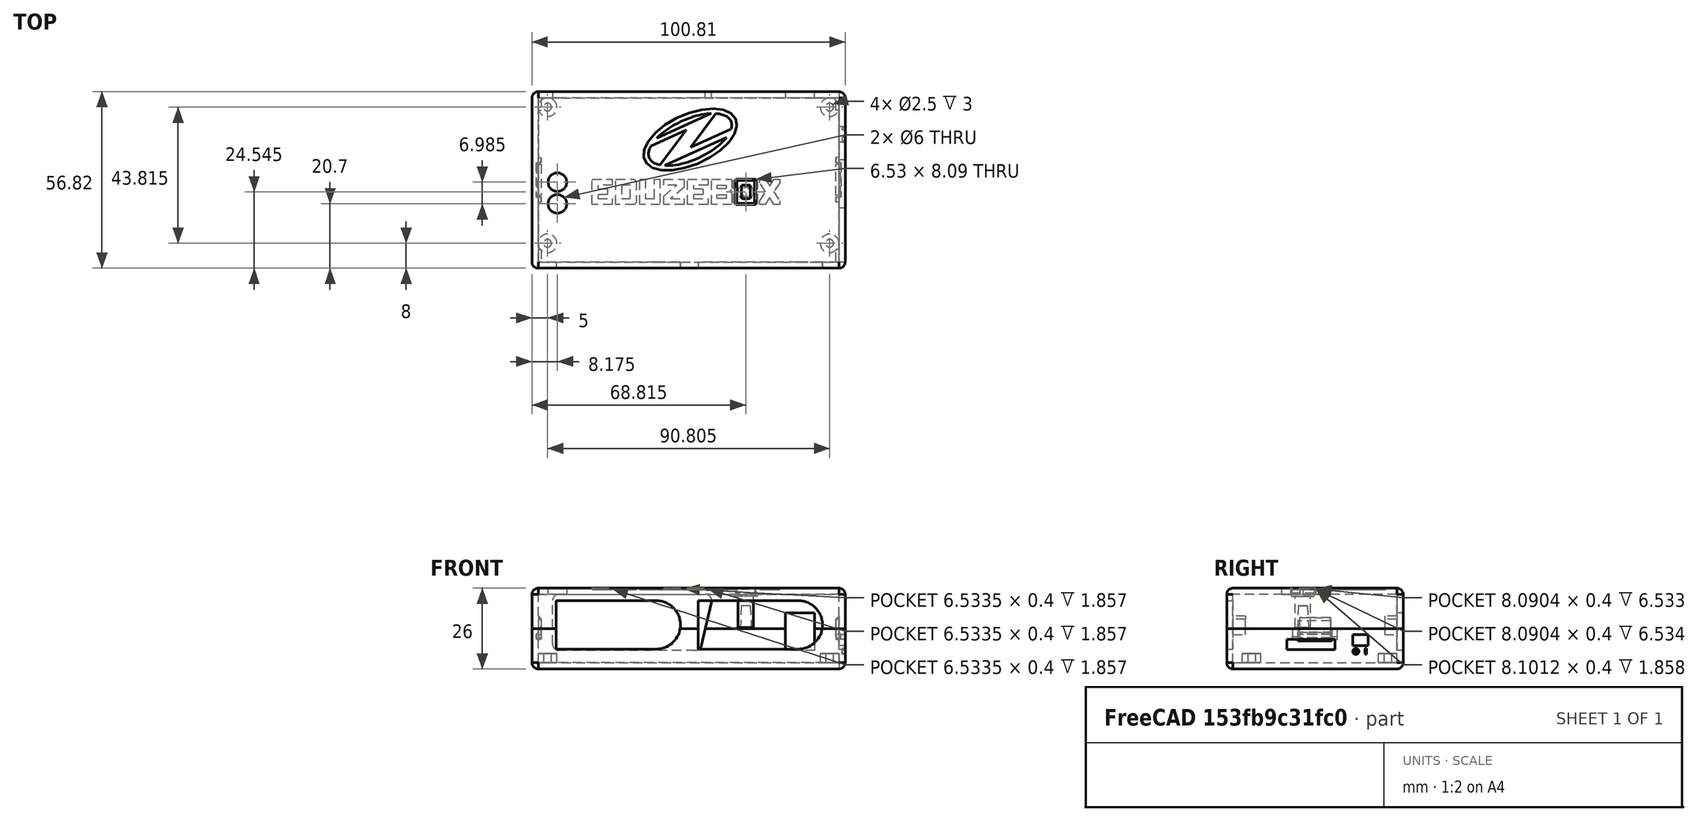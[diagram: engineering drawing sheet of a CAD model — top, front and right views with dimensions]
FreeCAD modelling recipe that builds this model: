
FCSTD DOCUMENT  (FreeCAD 0.18.4R)
Label: case
License: CreativeCommons Attribution-ShareAlike
LicenseURL: http://creativecommons.org/licenses/by-sa/4.0/
objects: Part::Extrusion×41, Part::Cut×38, Part::Part2DObjectPython×31, Part::FeaturePython×17, Part::Feature×11, Part::Fuse×10, Part::MultiFuse×6, Part::Thickness×2, Part::Chamfer×2, Part::Cone×1, Part::Cylinder×1
note: 160 computed .brp shape members not serialized (recipe doc carries the construction recipe); baked Part::Feature solids carry a one-line shape summary decoded from their .brp

FEATURE [Part::Part2DObjectPython] Block  label="PCB"  # Draft 2D object (typed FeaturePython)
  Placement = pos=(-88.9,107.95,0) rot=(0,0,1;0rad)
FEATURE [Part::Part2DObjectPython] Circle  # Draft 2D object (typed FeaturePython)
  FirstAngle = 0
  LastAngle = 0
  MakeFace = true
  Placement = pos=(2.54,2.54,-1.6) rot=(1,0,0;3.14159rad)
  Radius = 3
  Support = -> [Block]
FEATURE [Part::Extrusion] Extrude
  Base = -> Circle
  Dir = (0,0,-1)
  DirMode = 2
  FaceMakerClass = Part::FaceMakerBullseye
  LengthFwd = 3
  LengthRev = 0
  Solid = false
  Symmetric = false
FEATURE [Part::Part2DObjectPython] Circle001  # Draft 2D object (typed FeaturePython)
  FirstAngle = 0
  LastAngle = 0
  MakeFace = true
  Placement = pos=(2.54,2.54,-4.6) rot=(1,0,0;3.14159rad)
  Radius = 1.25
  Support = -> [Extrude]
FEATURE [Part::Extrusion] Extrude001  label="agujero"
  Base = -> Circle001
  Dir = (0,0,-1)
  DirMode = 2
  FaceMakerClass = Part::FaceMakerBullseye
  LengthFwd = -3
  LengthRev = 0
  Solid = false
  Symmetric = false
FEATURE [Part::Cut] Cut  label="Apoyo1"
  Base = -> Extrude
  Refine = true
  Tool = -> Extrude001
FEATURE [Part::FeaturePython] Clone  label="Apoyo2"  # Draft clone (typed FeaturePython)
  AttacherType = Attacher::AttachEngine3D
  Fuse = false
  Objects = -> [Cut]
  Placement = pos=(0,43.815,0) rot=(0,0,1;0rad)
  Scale = (1,1,1)
FEATURE [Part::FeaturePython] Clone001  label="Apoyo3"  # Draft clone (typed FeaturePython)
  AttacherType = Attacher::AttachEngine3D
  Fuse = false
  Objects = -> [Clone]
  Placement = pos=(90.805,43.815,0) rot=(0,0,1;0rad)
  Scale = (1,1,1)
FEATURE [Part::FeaturePython] Clone002  label="Apoyo4"  # Draft clone (typed FeaturePython)
  AttacherType = Attacher::AttachEngine3D
  Fuse = false
  Objects = -> [Clone001]
  Placement = pos=(90.805,0,0) rot=(0,0,1;0rad)
  Scale = (1,1,1)
FEATURE [Part::Part2DObjectPython] Rectangle  # Draft 2D object (typed FeaturePython)
  ChamferSize = 0
  Columns = 1
  FilletRadius = 0
  Height = 52.81
  Length = 96.805
  MakeFace = true
  Placement = pos=(-0.46,49.355,-4.6) rot=(1,0,0;3.14159rad)
  Rows = 1
FEATURE [Part::Extrusion] Extrude002
  Base = -> Rectangle
  Dir = (0,0,-1)
  DirMode = 2
  FaceMakerClass = Part::FaceMakerBullseye
  LengthFwd = -11
  LengthRev = 0
  Solid = false
  Symmetric = false
FEATURE [Part::Part2DObjectPython] Rectangle001  # Draft 2D object (typed FeaturePython)
  ChamferSize = 0
  Columns = 1
  FilletRadius = 0
  Height = 3.3
  Length = 15.5
  MakeFace = true
  Placement = pos=(98.345,13.93,-0.4) rot=(0.57735,0.57735,0.57735;2.0944rad)
  Rows = 1
FEATURE [Part::Extrusion] Extrude005  label="HuecoSD"
  Base = -> Rectangle001
  Dir = (1,0,0)
  DirMode = 2
  FaceMakerClass = Part::FaceMakerBullseye
  LengthFwd = -3
  LengthRev = 0
  Solid = false
  Symmetric = false
FEATURE [Part::Part2DObjectPython] Rectangle002  # Draft 2D object (typed FeaturePython)
  ChamferSize = 0
  Columns = 1
  FilletRadius = 0
  Height = 3.5
  Length = 5
  MakeFace = true
  Placement = pos=(98.345,35.06,0.9) rot=(0.57735,0.57735,0.57735;2.0944rad)
  Rows = 1
FEATURE [Part::Extrusion] Extrude006  label="HuecoOnOff"
  Base = -> Rectangle002
  Dir = (1,0,0)
  DirMode = 2
  FaceMakerClass = Part::FaceMakerBullseye
  LengthFwd = -3
  LengthRev = 0
  Solid = false
  Symmetric = false
FEATURE [Part::Part2DObjectPython] Rectangle003  # Draft 2D object (typed FeaturePython)
  ChamferSize = 0
  Columns = 1
  FilletRadius = 0
  Height = 12
  Length = 9.4
  MakeFace = true
  Placement = pos=(88.52,51.355,-0.6) rot=(0,0.707107,0.707107;3.14159rad)
  Rows = 1
FEATURE [Part::Extrusion] Extrude007  label="HuecoPower"
  Base = -> Rectangle003
  Dir = (0,1,-2e-16)
  DirMode = 2
  FaceMakerClass = Part::FaceMakerBullseye
  LengthFwd = -3
  LengthRev = 0
  Solid = false
  Symmetric = false
FEATURE [Part::Part2DObjectPython] Rectangle004  # Draft 2D object (typed FeaturePython)
  ChamferSize = 0
  Columns = 1
  FilletRadius = 0
  Height = 1.98134
  Length = 0.517414
  MakeFace = true
  Placement = pos=(98.345,39.0982,-1.9384) rot=(0.57735,0.57735,0.57735;2.0944rad)
  Rows = 1
FEATURE [Part::Extrusion] Extrude009  label="On"
  Base = -> Rectangle004
  Dir = (1,0,0)
  DirMode = 2
  FaceMakerClass = Part::FaceMakerBullseye
  LengthFwd = -1
  LengthRev = 0
  Solid = false
  Symmetric = false
FEATURE [Part::Part2DObjectPython] Circle002  # Draft 2D object (typed FeaturePython)
  FirstAngle = 0
  LastAngle = 0
  MakeFace = true
  Placement = pos=(98.345,36.126,-0.947734) rot=(0.57735,0.57735,0.57735;2.0944rad)
  Radius = 0.990671
FEATURE [Part::Extrusion] Extrude010  label="ExteriorOff"
  Base = -> Circle002
  Dir = (1,0,0)
  DirMode = 2
  FaceMakerClass = Part::FaceMakerBullseye
  LengthFwd = -1
  LengthRev = 0
  Solid = false
  Symmetric = false
FEATURE [Part::Part2DObjectPython] Circle003  # Draft 2D object (typed FeaturePython)
  FirstAngle = 0
  LastAngle = 0
  MakeFace = true
  Placement = pos=(98.345,36.126,-0.947734) rot=(0.57735,0.57735,0.57735;2.0944rad)
  Radius = 0.5
FEATURE [Part::Extrusion] Extrude011  label="InteriorOff"
  Base = -> Circle003
  Dir = (1,0,0)
  DirMode = 2
  FaceMakerClass = Part::FaceMakerBullseye
  LengthFwd = -1
  LengthRev = 0
  Solid = false
  Symmetric = false
FEATURE [Part::Part2DObjectPython] Rectangle005  # Draft 2D object (typed FeaturePython)
  ChamferSize = 0
  Columns = 1
  FilletRadius = 0
  Height = 52.81
  Length = 96.805
  MakeFace = true
  Placement = pos=(-0.46,-3.455,6.4) rot=(0,0,1;0rad)
  Rows = 1
FEATURE [Part::Extrusion] Extrude012
  Base = -> Rectangle005
  Dir = (0,0,1)
  DirMode = 2
  FaceMakerClass = Part::FaceMakerBullseye
  LengthFwd = 11
  LengthRev = 0
  Solid = false
  Symmetric = false
FEATURE [Part::Thickness] Thickness001
  Faces = -> Extrude012 [Face5]
  Intersection = false
  Join = 0
  Mode = 0
  SelfIntersection = false
  Value = 2
FEATURE [Part::Feature] Face003
  shape: bbox 55.45 x 2.007e-07 x 20.64 mm, 1 faces, 0 solids (baked)
FEATURE [Part::Extrusion] Extrude013  label="HuecoSCART2"
  Base = -> Face003
  Dir = (0,1,0)
  DirMode = 0
  FaceMakerClass = Part::FaceMakerBullseye
  LengthFwd = -2
  LengthRev = 0
  Solid = false
  Symmetric = false
FEATURE [Part::Feature] Face004
  shape: bbox 43.88 x 1.599e-05 x 17.16 mm, 1 faces, 0 solids (baked)
FEATURE [Part::Extrusion] Extrude014  label="HuecoPortA"
  Base = -> Face004
  Dir = (0,1,0)
  DirMode = 0
  FaceMakerClass = Part::FaceMakerBullseye
  LengthFwd = 2
  LengthRev = 0
  Solid = false
  Symmetric = false
FEATURE [Part::Thickness] Thickness
  Faces = -> Extrude002 [Face6]
  Intersection = false
  Join = 0
  Mode = 0
  SelfIntersection = false
  Value = 2
FEATURE [Part::FeaturePython] Clone003  label="HuecoPortB"  # Draft clone (typed FeaturePython)
  AttacherType = Attacher::AttachEngine3D
  Fuse = false
  Objects = -> [Extrude014]
  Placement = pos=(45.72,-7.62939e-08,2.98023e-09) rot=(0,0,1;0rad)
  Scale = (1,1,1)
FEATURE [Part::Cut] Cut001
  Base = -> Thickness
  Refine = true
  Tool = -> Extrude014
FEATURE [Part::Cut] Cut002
  Base = -> Cut001
  Refine = true
  Tool = -> Clone003
FEATURE [Part::Cut] Cut003
  Base = -> Cut002
  Refine = true
  Tool = -> Extrude005
FEATURE [Part::Cut] Cut004
  Base = -> Cut003
  Refine = true
  Tool = -> Extrude006
FEATURE [Part::Cut] Cut005
  Base = -> Cut004
  Refine = true
  Tool = -> Extrude010
FEATURE [Part::Cut] Cut006
  Base = -> Cut005
  Refine = true
  Tool = -> Extrude009
FEATURE [Part::Cut] Cut007
  Base = -> Cut006
  Refine = true
  Tool = -> Extrude007
FEATURE [Part::Cut] Cut008
  Base = -> Cut007
  Refine = true
  Tool = -> Extrude013
FEATURE [Part::Cut] Cut009
  Base = -> Thickness001
  Refine = true
  Tool = -> Extrude014
FEATURE [Part::Cut] Cut010
  Base = -> Cut009
  Refine = true
  Tool = -> Clone003
FEATURE [Part::Cut] Cut011
  Base = -> Cut010
  Refine = true
  Tool = -> Extrude007
FEATURE [Part::Cut] Cut012
  Base = -> Cut011
  Refine = true
  Tool = -> Extrude013
FEATURE [Part::Part2DObjectPython] Circle004  # Draft 2D object (typed FeaturePython)
  FirstAngle = 0
  LastAngle = 0
  MakeFace = true
  Placement = pos=(5.715,22.225,19.4) rot=(0,0,1;0rad)
  Radius = 2.5
  Support = -> [Cut012]
FEATURE [Part::Part2DObjectPython] Circle005  # Draft 2D object (typed FeaturePython)
  FirstAngle = 0
  LastAngle = 0
  MakeFace = true
  Placement = pos=(5.715,15.24,19.4) rot=(0,0,1;0rad)
  Radius = 2.5
FEATURE [Part::Extrusion] Extrude015  label="HuecoLEDRojo"
  Base = -> Circle004
  Dir = (0,0,1)
  DirMode = 2
  FaceMakerClass = Part::FaceMakerBullseye
  LengthFwd = -2
  LengthRev = 0
  Solid = false
  Symmetric = false
FEATURE [Part::Extrusion] Extrude016  label="HuecoLEDAzul"
  Base = -> Circle005
  Dir = (0,0,1)
  DirMode = 2
  FaceMakerClass = Part::FaceMakerBullseye
  LengthFwd = -2
  LengthRev = 0
  Solid = false
  Symmetric = false
FEATURE [Part::Cut] Cut013
  Base = -> Cut012
  Refine = true
  Tool = -> Extrude015
FEATURE [Part::Cut] Cut014
  Base = -> Cut013
  Refine = true
  Tool = -> Extrude016
FEATURE [Part::Part2DObjectPython] Wire  label="LogoU"  # Draft 2D object (typed FeaturePython)
  ChamferSize = 0
  Closed = true
  End = (31.5108,15.0742,19.4)
  FilletRadius = 0
  Length = 41.7617
  MakeFace = true
  Placement = pos=(31.5108,23.1754,19.4) rot=(0,0,1;0rad)
  Points = (8) [(0,0,0),(1.85748,0,0),(1.86285,-6.24368,0),(4.68122,-6.24368,0),(4.68122,0,0),(6.5387,0,0),(6.5387,-8.10116,0),(0,-8.10116,0)]
  Start = (31.5108,23.1754,19.4)
  Subdivisions = 0
FEATURE [Part::Part2DObjectPython] Wire001  label="LogoZ"  # Draft 2D object (typed FeaturePython)
  ChamferSize = 0
  Closed = true
  End = (39.2449,21.3179,19.4)
  FilletRadius = 0
  Length = 41.9129
  MakeFace = true
  Placement = pos=(39.2449,23.1754,19.4) rot=(0,0,1;0rad)
  Points = (10) [(0,0,0),(6.53352,0,0),(6.53352,-2.67345,0),(2.22794,-6.23293,0),(6.53352,-6.23293,0),(6.53352,-8.09041,0),(0,-8.09041,0),(0,-5.41676,0),+2 more]
  Start = (39.2449,23.1754,19.4)
  Subdivisions = 0
FEATURE [Part::Part2DObjectPython] Wire002  label="LogoE2"  # Draft 2D object (typed FeaturePython)
  ChamferSize = 0
  Closed = true
  End = (46.9353,15.085,19.4)
  FilletRadius = 0
  Length = 44.6982
  MakeFace = true
  Placement = pos=(46.9353,23.1754,19.4) rot=(0,0,1;0rad)
  Points = (12) [(0,0,0),(6.53352,0,0),(6.53352,-1.85748,0),(1.85767,-1.85748,0),(1.85767,-3.11915,0),(4.97663,-3.11915,0),(4.97663,-4.97125,0),(1.93272,-4.97125,0),+4 more]
  Start = (46.9353,23.1754,19.4)
  Subdivisions = 0
FEATURE [Part::Part2DObjectPython] Wire003  label="LogoB0"  # Draft 2D object (typed FeaturePython)
  ChamferSize = 0
  Closed = true
  End = (54.6335,15.085,19.4)
  FilletRadius = 0
  Length = 29.7435
  MakeFace = true
  Placement = pos=(54.6335,23.1754,19.4) rot=(0,0,1;0rad)
  Points = (7) [(0,0,0),(6.53352,0,0),(6.54964,-3.39824,0),(5.93771,-4.01036,0),(6.53352,-4.62229,0),(6.53352,-8.09041,0),(0,-8.09041,0)]
  Start = (54.6335,23.1754,19.4)
  Subdivisions = 0
FEATURE [Part::Part2DObjectPython] Wire004  label="LogoB1"  # Draft 2D object (typed FeaturePython)
  ChamferSize = 0
  Closed = true
  End = (56.4912,20.0563,19.4)
  FilletRadius = 0
  Length = 8.16008
  MakeFace = true
  Placement = pos=(56.4912,21.3179,19.4) rot=(0,0,1;0rad)
  Points = (4) [(0,0,0),(2.81837,0,0),(2.81837,-1.26167,0),(0,-1.26167,0)]
  Start = (56.4912,21.3179,19.4)
  Subdivisions = 0
FEATURE [Part::Part2DObjectPython] Wire005  label="LogoB2"  # Draft 2D object (typed FeaturePython)
  ChamferSize = 0
  Closed = true
  End = (56.4912,16.9425,19.4)
  FilletRadius = 0
  Length = 8.16008
  MakeFace = true
  Placement = pos=(56.4912,18.2042,19.4) rot=(0,0,1;0rad)
  Points = (4) [(0,0,0),(2.81837,0,0),(2.81837,-1.26167,0),(0,-1.26167,0)]
  Start = (56.4912,18.2042,19.4)
  Subdivisions = 0
FEATURE [Part::Part2DObjectPython] Wire006  label="LogoX"  # Draft 2D object (typed FeaturePython)
  ChamferSize = 0
  Closed = true
  End = (70.7859,22.0694,19.4)
  FilletRadius = 0
  Length = 36.5598
  MakeFace = true
  Placement = pos=(70.7859,23.1862,19.4) rot=(0,0,1;0rad)
  Points = (16) [(0,0,0),(1.85748,0,0),(3.3017,-2.21719,0),(4.68142,0,0),(6.5389,0,0),(6.5389,-1.11675,0),(4.53112,-4.01574,0),(6.5389,-6.98441,0),(6.5389,-8.10116,0),+7 more]
  Start = (70.7859,23.1862,19.4)
  Subdivisions = 0
FEATURE [Part::Part2DObjectPython] Rectangle006  label="LogoD1"  # Draft 2D object (typed FeaturePython)
  ChamferSize = 0
  Columns = 1
  FilletRadius = 0
  Height = 4.37545
  Length = 2.81837
  MakeFace = true
  Placement = pos=(25.727,16.9425,19.4) rot=(0,0,1;0rad)
  Rows = 1
FEATURE [Part::Feature] Face  label="LogoD0"
  Placement = pos=(12.3152,-43.294,-3.8147e-07) rot=(0,0,1;0rad)
  shape: bbox 7.217 x 8.924 x 2e-07 mm, 1 faces, 0 solids (baked)
FEATURE [Part::Part2DObjectPython] Clone2D  label="LogoE1"  # Draft 2D object (typed FeaturePython)
  Fuse = false
  Objects = -> [Wire002]
  Placement = pos=(16.1868,23.1754,19.4) rot=(0,0,1;0rad)
  Scale = (1,1,1)
FEATURE [Part::Extrusion] Extrude018  label="LogoE1_v"
  Base = -> Clone2D
  Dir = (0,0,1)
  DirMode = 2
  FaceMakerClass = Part::FaceMakerBullseye
  LengthFwd = -0.4
  LengthRev = 0
  Placement = pos=(0.680956,0,0) rot=(0,0,1;0rad)
  Solid = false
  Symmetric = false
FEATURE [Part::Extrusion] Extrude019  label="LogoD0_v"
  Base = -> Face
  Dir = (0,0,-1)
  DirMode = 0
  FaceMakerClass = Part::FaceMakerBullseye
  LengthFwd = 0.4
  LengthRev = 0
  Placement = pos=(0.680956,0,0) rot=(0,0,1;0rad)
  Solid = false
  Symmetric = false
FEATURE [Part::Extrusion] Extrude020  label="LogoD1_v"
  Base = -> Rectangle006
  Dir = (0,0,1)
  DirMode = 2
  FaceMakerClass = Part::FaceMakerBullseye
  LengthFwd = -0.4
  LengthRev = 0
  Placement = pos=(0.680956,0,0) rot=(0,0,1;0rad)
  Solid = false
  Symmetric = false
FEATURE [Part::Extrusion] Extrude021  label="LogoU_v"
  Base = -> Wire
  Dir = (0,0,1)
  DirMode = 2
  FaceMakerClass = Part::FaceMakerBullseye
  LengthFwd = -0.4
  LengthRev = 0
  Placement = pos=(0.680956,0,0) rot=(0,0,1;0rad)
  Solid = false
  Symmetric = false
FEATURE [Part::Extrusion] Extrude022  label="LogoZ_v"
  Base = -> Wire001
  Dir = (0,0,1)
  DirMode = 2
  FaceMakerClass = Part::FaceMakerBullseye
  LengthFwd = -0.4
  LengthRev = 0
  Placement = pos=(0.680956,0,0) rot=(0,0,1;0rad)
  Solid = false
  Symmetric = false
FEATURE [Part::Extrusion] Extrude023  label="LogoE2_v"
  Base = -> Wire002
  Dir = (0,0,1)
  DirMode = 2
  FaceMakerClass = Part::FaceMakerBullseye
  LengthFwd = -0.4
  LengthRev = 0
  Placement = pos=(0.680956,0,0) rot=(0,0,1;0rad)
  Solid = false
  Symmetric = false
FEATURE [Part::Extrusion] Extrude024  label="LogoB0_v"
  Base = -> Wire003
  Dir = (0,0,1)
  DirMode = 2
  FaceMakerClass = Part::FaceMakerBullseye
  LengthFwd = -0.4
  LengthRev = 0
  Placement = pos=(0.680956,0,0) rot=(0,0,1;0rad)
  Solid = false
  Symmetric = false
FEATURE [Part::Extrusion] Extrude025  label="LogoB1_v"
  Base = -> Wire004
  Dir = (0,0,1)
  DirMode = 2
  FaceMakerClass = Part::FaceMakerBullseye
  LengthFwd = -0.4
  LengthRev = 0
  Placement = pos=(0.680956,0,0) rot=(0,0,1;0rad)
  Solid = false
  Symmetric = false
FEATURE [Part::Extrusion] Extrude026  label="LogoB2_v"
  Base = -> Wire005
  Dir = (0,0,1)
  DirMode = 2
  FaceMakerClass = Part::FaceMakerBullseye
  LengthFwd = -0.4
  LengthRev = 0
  Placement = pos=(0.680956,0,0) rot=(0,0,1;0rad)
  Solid = false
  Symmetric = false
FEATURE [Part::Extrusion] Extrude027  label="LogoX_v"
  Base = -> Wire006
  Dir = (0,0,1)
  DirMode = 2
  FaceMakerClass = Part::FaceMakerBullseye
  LengthFwd = -0.4
  LengthRev = 0
  Solid = false
  Symmetric = false
FEATURE [Part::Part2DObjectPython] Rectangle007  label="LogoO"  # Draft 2D object (typed FeaturePython)
  ChamferSize = 0
  Columns = 1
  FilletRadius = 0
  Height = 8.09041
  Length = 6.53352
  MakeFace = true
  Placement = pos=(63.0881,15.0398,19.4) rot=(0,0,1;0rad)
  Rows = 1
FEATURE [Part::Part2DObjectPython] Clone2D002  label="Rectangle008 (2D)"  # Draft 2D object (typed FeaturePython)
  Fuse = false
  Placement = pos=(64.9457,16.8973,19.4) rot=(0,0,1;0rad)
  Scale = (1,1,1)
FEATURE [Part::Extrusion] Extrude028  label="LogoO_v"
  Base = -> Rectangle007
  Dir = (0,0,1)
  DirMode = 2
  FaceMakerClass = Part::FaceMakerBullseye
  LengthFwd = -2
  LengthRev = 0
  Solid = false
  Symmetric = false
FEATURE [Part::Cut] Cut015
  Base = -> Cut014
  Refine = true
  Tool = -> Extrude018
FEATURE [Part::Cut] Cut016
  Base = -> Cut015
  Refine = true
  Tool = -> Extrude019
FEATURE [Part::Fuse] Fusion
  Base = -> Cut016
  Refine = true
  Tool = -> Extrude020
FEATURE [Part::Cut] Cut017
  Base = -> Fusion
  Refine = true
  Tool = -> Extrude021
FEATURE [Part::Cut] Cut018
  Base = -> Cut017
  Refine = true
  Tool = -> Extrude022
FEATURE [Part::Cut] Cut019
  Base = -> Cut018
  Refine = true
  Tool = -> Extrude023
FEATURE [Part::Cut] Cut020
  Base = -> Cut019
  Refine = true
  Tool = -> Extrude024
FEATURE [Part::Fuse] Fusion001
  Base = -> Cut020
  Refine = true
  Tool = -> Extrude025
FEATURE [Part::Fuse] Fusion002
  Base = -> Fusion001
  Refine = true
  Tool = -> Extrude026
FEATURE [Part::Cut] Cut021
  Base = -> Fusion002
  Refine = true
  Tool = -> Extrude028
FEATURE [Part::Cut] Cut022
  Base = -> Cut021
  Refine = true
  Tool = -> Extrude027
FEATURE [Part::Fuse] Fusion003
  Base = -> Cut008
  Refine = true
  Tool = -> Extrude011
FEATURE [Part::Fuse] Fusion004
  Base = -> Fusion003
  Refine = true
  Tool = -> Cut
FEATURE [Part::Fuse] Fusion005
  Base = -> Fusion004
  Refine = true
  Tool = -> Clone
FEATURE [Part::Fuse] Fusion006
  Base = -> Fusion005
  Refine = true
  Tool = -> Clone001
FEATURE [Part::Fuse] Fusion007
  Base = -> Fusion006
  Refine = true
  Tool = -> Clone002
FEATURE [Part::Feature] Face006
  shape: bbox 2.313 x 2e-07 x 7.787 mm, 1 faces, 0 solids (baked)
FEATURE [Part::Extrusion] Extrude029  label="LenguetaDer"
  Base = -> Face006
  Dir = (0,1,0)
  DirMode = 0
  FaceMakerClass = Part::FaceMakerBullseye
  LengthFwd = 10
  LengthRev = 0
  Solid = false
  Symmetric = false
FEATURE [Part::FeaturePython] Clone004  label="LenguetaIzq"  # Draft clone (typed FeaturePython)
  AttacherType = Attacher::AttachEngine3D
  Fuse = false
  Objects = -> [Extrude029]
  Placement = pos=(95.88,45.9,-4.9e-14) rot=(0,0,1;3.14159rad)
  Scale = (1,1,1)
FEATURE [Part::Fuse] Fusion008
  Base = -> Cut022
  Refine = true
  Tool = -> Extrude029
FEATURE [Part::Fuse] Fusion009  label="Superior0"
  Base = -> Fusion008
  Refine = true
  Tool = -> Clone004
FEATURE [Part::Cut] Cut023
  Base = -> Fusion007
  Refine = true
  Tool = -> Extrude029
FEATURE [Part::Cut] Cut024
  Base = -> Cut023
  Refine = true
  Tool = -> Clone004
FEATURE [Part::Feature] Face007
  shape: bbox 2e-07 x 2.2 x 3.85 mm, 1 faces, 0 solids (baked)
FEATURE [Part::Extrusion] Extrude030
  Base = -> Face007
  Dir = (1,0,0)
  DirMode = 0
  FaceMakerClass = Part::FaceMakerBullseye
  LengthFwd = 1
  LengthRev = 0
  Solid = false
  Symmetric = false
FEATURE [Part::Chamfer] Chamfer
  Base = -> Extrude030
  Edges = 1 edges r=0.99: [Edge7]
  Placement = pos=(0,-0.2,0) rot=(0,0,1;0rad)
FEATURE [Part::FeaturePython] Clone005  label="Chamfer001"  # Draft clone (typed FeaturePython)
  AttacherType = Attacher::AttachEngine3D
  Fuse = false
  Objects = -> [Chamfer]
  Placement = pos=(0,12.2,0) rot=(0,0,1;0rad)
  Scale = (1,1,1)
FEATURE [Part::FeaturePython] Clone006  label="Chamfer002"  # Draft clone (typed FeaturePython)
  AttacherType = Attacher::AttachEngine3D
  Fuse = false
  Objects = -> [Chamfer]
  Placement = pos=(95.885,33.7,4.3e-14) rot=(0,0,1;3.14159rad)
  Scale = (1,1,1)
FEATURE [Part::FeaturePython] Clone007  label="Chamfer003"  # Draft clone (typed FeaturePython)
  AttacherType = Attacher::AttachEngine3D
  Fuse = false
  Objects = -> [Clone006]
  Placement = pos=(95.895,46.1,4.3e-14) rot=(0,0,1;3.14159rad)
  Scale = (1,1,1)
FEATURE [Part::MultiFuse] Fusion010
  Refine = true
  Shapes = -> [Cut024,Clone005,Chamfer,Clone006,Clone007]
FEATURE [Part::Feature] Face008
  shape: bbox 0.5602 x 2e-07 x 2.201 mm, 1 faces, 0 solids (baked)
FEATURE [Part::Extrusion] Extrude031  label="Espaciador"
  Base = -> Face008
  Dir = (0,1,0)
  DirMode = 0
  FaceMakerClass = Part::FaceMakerBullseye
  LengthFwd = -0.2
  LengthRev = 0
  Placement = pos=(95.88,35.7,4.9e-14) rot=(0,0,1;3.14159rad)
  Solid = false
  Symmetric = false
FEATURE [Part::FeaturePython] Clone008  label="Espaciador001"  # Draft clone (typed FeaturePython)
  AttacherType = Attacher::AttachEngine3D
  Fuse = false
  Objects = -> [Extrude031]
  Placement = pos=(1e-16,10.2,0) rot=(0,0,1;0rad)
  Scale = (1,1,1)
FEATURE [Part::FeaturePython] Clone009  label="Espaciador002"  # Draft clone (typed FeaturePython)
  AttacherType = Attacher::AttachEngine3D
  Fuse = false
  Objects = -> [Extrude031]
  Scale = (1,1,1)
FEATURE [Part::FeaturePython] Clone010  label="Espaciador003"  # Draft clone (typed FeaturePython)
  AttacherType = Attacher::AttachEngine3D
  Fuse = false
  Objects = -> [Extrude031]
  Placement = pos=(95.88,45.9,4.9e-14) rot=(0,0,1;3.14159rad)
  Scale = (1,1,1)
FEATURE [Part::Cut] Cut025
  Base = -> Fusion010
  Refine = true
  Tool = -> Extrude031
FEATURE [Part::Cut] Cut026
  Base = -> Cut025
  Refine = true
  Tool = -> Clone008
FEATURE [Part::Cut] Cut027
  Base = -> Cut026
  Refine = true
  Tool = -> Clone009
FEATURE [Part::Cut] Cut028  label="Inferior0"
  Base = -> Cut027
  Refine = true
  Tool = -> Clone010
FEATURE [Part::Part2DObjectPython] Rectangle008  # Draft 2D object (typed FeaturePython)
  ChamferSize = 0
  Columns = 1
  FilletRadius = 0
  Height = 6
  Length = 4
  MakeFace = true
  Placement = pos=(96.345,49.355,4.4) rot=(0.57735,-0.57735,-0.57735;2.0944rad)
  Rows = 1
FEATURE [Part::Extrusion] Extrude032
  Base = -> Rectangle008
  Dir = (-1,0,0)
  DirMode = 2
  FaceMakerClass = Part::FaceMakerBullseye
  LengthFwd = 1
  LengthRev = 0
  Solid = false
  Symmetric = false
FEATURE [Part::Chamfer] Chamfer001  label="Chamfer004"
  Base = -> Extrude032
  Edges = 1 edges r=0.99: [Edge10]
FEATURE [Part::FeaturePython] Clone011  label="Chamfer005"  # Draft clone (typed FeaturePython)
  AttacherType = Attacher::AttachEngine3D
  Fuse = false
  Objects = -> [Chamfer001]
  Placement = pos=(0,-48.81,0) rot=(0,0,1;0rad)
  Scale = (1,1,1)
FEATURE [Part::FeaturePython] Clone012  label="Chamfer006"  # Draft clone (typed FeaturePython)
  AttacherType = Attacher::AttachEngine3D
  Fuse = false
  Objects = -> [Chamfer001]
  Placement = pos=(95.885,45.9,0) rot=(0,0,1;3.14159rad)
  Scale = (1,1,1)
FEATURE [Part::FeaturePython] Clone013  label="Chamfer007"  # Draft clone (typed FeaturePython)
  AttacherType = Attacher::AttachEngine3D
  Fuse = false
  Objects = -> [Clone012]
  Placement = pos=(95.885,94.71,0) rot=(0,0,1;3.14159rad)
  Scale = (1,1,1)
FEATURE [Part::MultiFuse] Fusion011  label="Superior001"
  Refine = true
  Shapes = -> [Fusion009,Chamfer001,Clone011,Clone012,Clone013]
FEATURE [Part::Part2DObjectPython] Circle006  # Draft 2D object (typed FeaturePython)
  FirstAngle = 0
  LastAngle = 0
  MakeFace = true
  Placement = pos=(5.715,22.225,19.4) rot=(0,0,1;0rad)
  Radius = 3
FEATURE [Part::Part2DObjectPython] Circle007  # Draft 2D object (typed FeaturePython)
  FirstAngle = 0
  LastAngle = 0
  MakeFace = true
  Placement = pos=(5.715,15.24,19.4) rot=(0,0,1;0rad)
  Radius = 3
FEATURE [Part::Extrusion] Extrude033  label="HuecoLEDAzul+"
  Base = -> Circle007
  Dir = (0,0,1)
  DirMode = 2
  FaceMakerClass = Part::FaceMakerBullseye
  LengthFwd = -3
  LengthRev = 0
  Solid = false
  Symmetric = false
FEATURE [Part::Extrusion] Extrude034  label="HuecoLEDRojo+"
  Base = -> Circle006
  Dir = (0,0,1)
  DirMode = 2
  FaceMakerClass = Part::FaceMakerBullseye
  LengthFwd = -3
  LengthRev = 0
  Solid = false
  Symmetric = false
FEATURE [Part::Cut] Cut029
  Base = -> Fusion011
  Refine = true
  Tool = -> Extrude033
FEATURE [Part::Cut] Cut030  label="Superior002"
  Base = -> Cut029
  Refine = true
  Tool = -> Extrude034
FEATURE [Part::Part2DObjectPython] Wire008  # Draft 2D object (typed FeaturePython)
  ChamferSize = 0
  Closed = true
  End = (96.145,28.15,2.42216)
  FilletRadius = 0
  Length = 6.66696
  MakeFace = true
  Points = (4) [(97.045,28.15,3.32216),(97.045,28.15,4.48284),(96.145,28.15,5.38284),(96.145,28.15,2.42216)]
  Start = (97.045,28.15,3.32216)
  Subdivisions = 0
FEATURE [Part::Extrusion] Extrude035  label="AhuecaDer"
  Base = -> Wire008
  Dir = (0,1,0)
  DirMode = 0
  FaceMakerClass = Part::FaceMakerBullseye
  LengthFwd = -11
  LengthRev = 0
  Placement = pos=(0,0.3,0) rot=(0,0,1;0rad)
  Solid = false
  Symmetric = false
FEATURE [Part::FeaturePython] Clone014  label="AhuecaIzq"  # Draft clone (typed FeaturePython)
  AttacherType = Attacher::AttachEngine3D
  Fuse = false
  Objects = -> [Extrude035]
  Placement = pos=(95.8812,0.3,7.80375) rot=(0,1,0;3.14159rad)
  Scale = (1,1,1)
FEATURE [Part::Part2DObjectPython] Rectangle009  # Draft 2D object (typed FeaturePython)
  ChamferSize = 0
  Columns = 1
  FilletRadius = 0
  Height = 7.29041
  Length = 5.73352
  MakeFace = true
  Placement = pos=(63.4881,15.4398,19.4) rot=(0,0,1;0rad)
  Rows = 1
FEATURE [Part::Extrusion] Extrude036
  Base = -> Rectangle009
  Dir = (0,0,1)
  DirMode = 2
  FaceMakerClass = Part::FaceMakerBullseye
  LengthFwd = -1.6
  LengthRev = 0
  Solid = false
  Symmetric = false
FEATURE [Part::Feature] Face009
  shape: bbox 8.507 x 2e-07 x 1.1 mm, 1 faces, 0 solids (baked)
FEATURE [Part::Extrusion] Extrude037
  Base = -> Face009
  Dir = (0,1,0)
  DirMode = 0
  FaceMakerClass = Part::FaceMakerBullseye
  LengthFwd = 7.29
  LengthRev = 0
  Solid = false
  Symmetric = false
FEATURE [Part::Cone] Cone
  Angle = 360
  AttacherType = Attacher::AttachEngine3D
  Height = 8
  Placement = pos=(66.3549,19.0848,13.75) rot=(1,0,0;3.14159rad)
  Radius1 = 1.45
  Radius2 = 1.8
FEATURE [Part::Cylinder] Cylinder
  Angle = 360
  AttacherType = Attacher::AttachEngine3D
  Height = 11.9
  Placement = pos=(66.3549,19.0848,6.8) rot=(0,0,1;0rad)
  Radius = 2.5
FEATURE [Part::Cut] Cut033
  Base = -> Cylinder
  Refine = true
  Tool = -> Cone
FEATURE [Part::MultiFuse] Fusion012
  Refine = true
  Shapes = -> [Extrude036,Cut033,Extrude037]
FEATURE [Part::Extrusion] Extrude038
  Base = -> Clone2D002
  Dir = (0,0,1)
  DirMode = 2
  FaceMakerClass = Part::FaceMakerBullseye
  LengthFwd = -0.2
  LengthRev = 0
  Solid = false
  Symmetric = false
FEATURE [Part::Cut] Cut034  label="RESET"
  Base = -> Fusion012
  Refine = true
  Tool = -> Extrude038
FEATURE [Part::Part2DObjectPython] Ellipse  label="EllExt"  # Draft 2D object (typed FeaturePython)
  FirstAngle = 0
  LastAngle = 0
  MajorRadius = 16.09
  MakeFace = true
  MinorRadius = 8.07
  Placement = pos=(48.4435,35.9407,19.4) rot=(0,0,1;0.427606rad)
FEATURE [Part::Feature] Face010  label="Zu"
  Placement = pos=(28.5348,-41.7553,0) rot=(0,0,1;0.427606rad)
  shape: bbox 20.05 x 10.45 x 2e-07 mm, 1 faces, 0 solids (baked)
FEATURE [Part::Feature] Face011  label="Zl"
  Placement = pos=(28.5348,-41.7553,0) rot=(0,0,1;0.427606rad)
  shape: bbox 17.28 x 16.24 x 2e-07 mm, 1 faces, 0 solids (baked)
FEATURE [Part::Feature] Face012  label="Zb"
  Placement = pos=(28.5348,-41.7553,0) rot=(0,0,1;0.427606rad)
  shape: bbox 23.01 x 12.29 x 2e-07 mm, 1 faces, 0 solids (baked)
FEATURE [Part::Feature] Face013  label="Zr"
  Placement = pos=(28.5348,-41.7553,0) rot=(0,0,1;0.427606rad)
  shape: bbox 18.19 x 16.14 x 2e-07 mm, 1 faces, 0 solids (baked)
FEATURE [Part::Extrusion] Extrude039  label="EllExtV"
  Base = -> Ellipse
  Dir = (0,0,1)
  DirMode = 2
  FaceMakerClass = Part::FaceMakerBullseye
  LengthFwd = -0.4
  LengthRev = 0
  Solid = false
  Symmetric = false
FEATURE [Part::Extrusion] Extrude040  label="ZtV"
  Base = -> Face010
  Dir = (0,0,-1)
  DirMode = 0
  FaceMakerClass = Part::FaceMakerBullseye
  LengthFwd = 0.4
  LengthRev = 0
  Solid = false
  Symmetric = false
FEATURE [Part::Extrusion] Extrude041  label="ZlV"
  Base = -> Face011
  Dir = (0,0,-1)
  DirMode = 0
  FaceMakerClass = Part::FaceMakerBullseye
  LengthFwd = 0.4
  LengthRev = 0
  Solid = false
  Symmetric = false
FEATURE [Part::Extrusion] Extrude042  label="ZbV"
  Base = -> Face012
  Dir = (0,0,-1)
  DirMode = 0
  FaceMakerClass = Part::FaceMakerBullseye
  LengthFwd = 0.4
  LengthRev = 0
  Solid = false
  Symmetric = false
FEATURE [Part::Extrusion] Extrude043  label="ZrV"
  Base = -> Face013
  Dir = (0,0,-1)
  DirMode = 0
  FaceMakerClass = Part::FaceMakerBullseye
  LengthFwd = 0.4
  LengthRev = 0
  Solid = false
  Symmetric = false
FEATURE [Part::Cut] Cut035
  Base = -> Cut030
  Refine = true
  Tool = -> Extrude039
FEATURE [Part::MultiFuse] Fusion013  label="Superior003"
  Refine = true
  Shapes = -> [Cut035,Extrude041,Extrude043,Extrude040,Extrude042]
FEATURE [Part::FeaturePython] Clone015  label="HuecoSCART3"  # Draft clone (typed FeaturePython)
  AttacherType = Attacher::AttachEngine3D
  Fuse = false
  Objects = -> [Extrude013]
  Placement = pos=(-1,0,0) rot=(0,0,1;0rad)
  Scale = (1,1,1)
FEATURE [Part::Cut] Cut037  label="Superior"
  Base = -> Fusion013
  Refine = true
  Tool = -> Clone015
FEATURE [Part::Cut] Cut038
  Base = -> Cut028
  Refine = true
  Tool = -> Clone015
FEATURE [Part::MultiFuse] Fusion014  label="Ahuecadores"
  Refine = true
  Shapes = -> [Clone014,Extrude035]
FEATURE [Part::Cut] Cut039  label="Inferior001"
  Base = -> Cut038
  Refine = true
  Tool = -> Fusion014
FEATURE [Part::Part2DObjectPython] Rectangle010  # Draft 2D object (typed FeaturePython)
  ChamferSize = 0
  Columns = 1
  FilletRadius = 0
  Height = 11
  Length = 2
  MakeFace = true
  Placement = pos=(94.345,17.45,6.4) rot=(0,0,1;0rad)
  Rows = 1
FEATURE [Part::Extrusion] Extrude044  label="AhuecadorB1"
  Base = -> Rectangle010
  Dir = (0,0,1)
  DirMode = 2
  FaceMakerClass = Part::FaceMakerBullseye
  LengthFwd = -4
  LengthRev = 0
  Solid = false
  Symmetric = false
FEATURE [Part::FeaturePython] Clone016  label="AhuecadorB2"  # Draft clone (typed FeaturePython)
  AttacherType = Attacher::AttachEngine3D
  Fuse = false
  Objects = -> [Extrude044]
  Placement = pos=(-94.81,6.231e-12,-4.3e-14) rot=(0,0,1;0rad)
  Scale = (1,1,1)
FEATURE [Part::MultiFuse] Fusion015  label="AhuecadoresB"
  Refine = true
  Shapes = -> [Extrude044,Clone016]
FEATURE [Part::Cut] Cut040  label="Inferior"
  Base = -> Cut039
  Refine = true
  Tool = -> Fusion015
